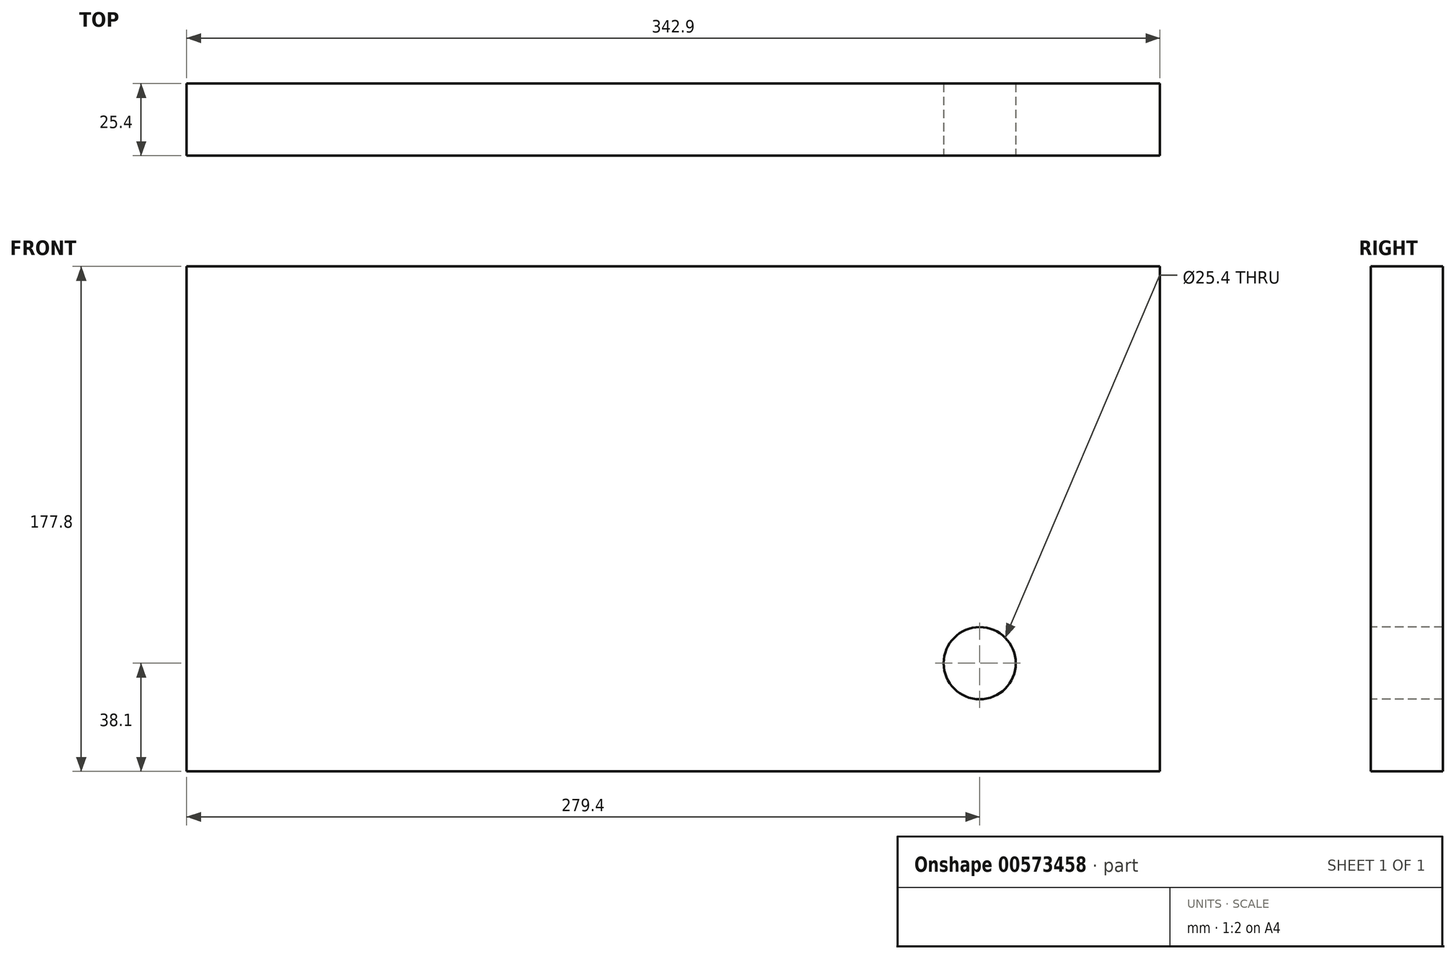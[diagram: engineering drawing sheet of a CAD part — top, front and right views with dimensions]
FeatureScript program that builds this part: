
annotation { "Feature Type Name" : "Feature", "Feature Type Description" : "" }
export const myFeature = defineFeature(function(context is Context, id is Id, definition is map)
    precondition{}
    {
        {
            var Q0;
            Q0=qCreatedBy(makeId("Front.planeOp"),FACE);
            var sketch = newSketch(context, id + "F0", { "sketchPlane" : qUnion([Q0])});
            skPoint(sketch, "E0.middle", {"position": v(0, 0) * mm});
            skLineSegment(sketch, "E1.bottom", {"start": v(-171.45, -88.9) * mm, "end": v(171.45, -88.9) * mm});
            skLineSegment(sketch, "E1.top", {"start": v(-171.45, 88.9) * mm, "end": v(171.45, 88.9) * mm});
            skLineSegment(sketch, "E1.left", {"start": v(-171.45, -88.9) * mm, "end": v(-171.45, 88.9) * mm});
            skLineSegment(sketch, "E1.right", {"start": v(171.45, -88.9) * mm, "end": v(171.45, 88.9) * mm});
            skSolve(sketch);
        }
        {
            var Q0;
            Q0=makeQuery(id+"F0.imprint","IMPRINT",FACE,{"disambiguationData":[TD([[makeQuery(id+"F0.imprint","IMPRINT",EDGE,{"derivedFrom":sQuery(id+"F0.wireOp",EDGE,"E1.bottom")}),1.0]])]});
            extrude(context, id + "F1", {"entities" : qUnion([Q0]), "depth" : 25.4 * mm, "offsetDistance" : 25.4 * mm});
        }
        {
            var Q0;
            Q0=makeQuery(id+"F1.opExtrude","CAP_FACE",FACE,{"disambiguationData":[OSD([sQuery(id+"F0.wireOp",EDGE,"E0.bottom"),sQuery(id+"F0.wireOp",EDGE,"E0.left"),sQuery(id+"F0.wireOp",EDGE,"E0.right"),sQuery(id+"F0.wireOp",EDGE,"E1.bottom"),sQuery(id+"F0.wireOp",EDGE,"E1.top"),sQuery(id+"F0.wireOp",EDGE,"E1.left"),sQuery(id+"F0.wireOp",EDGE,"E1.right")])],"isStart":false});
            var sketch = newSketch(context, id + "F2", { "sketchPlane" : qUnion([Q0])});
            skCircle(sketch, "E2", {"center": v(107.95, -50.8) * mm, "radius": 12.7 * mm});
            skSolve(sketch);
        }
        {
            var Q0;
            Q0=makeQuery(id+"F2.imprint","IMPRINT",FACE,{"disambiguationData":[TD([[makeQuery(id+"F2.imprint","IMPRINT",EDGE,{"derivedFrom":sQuery(id+"F2.wireOp",EDGE,"E2")}),1.0]])]});
            extrude(context, id + "F3", {"entities" : qUnion([Q0]), "operationType" : NewBodyOperationType.REMOVE, "oppositeDirection" : true, "depth" : 25.4 * mm, "offsetDistance" : 25.4 * mm});
        }
    });
